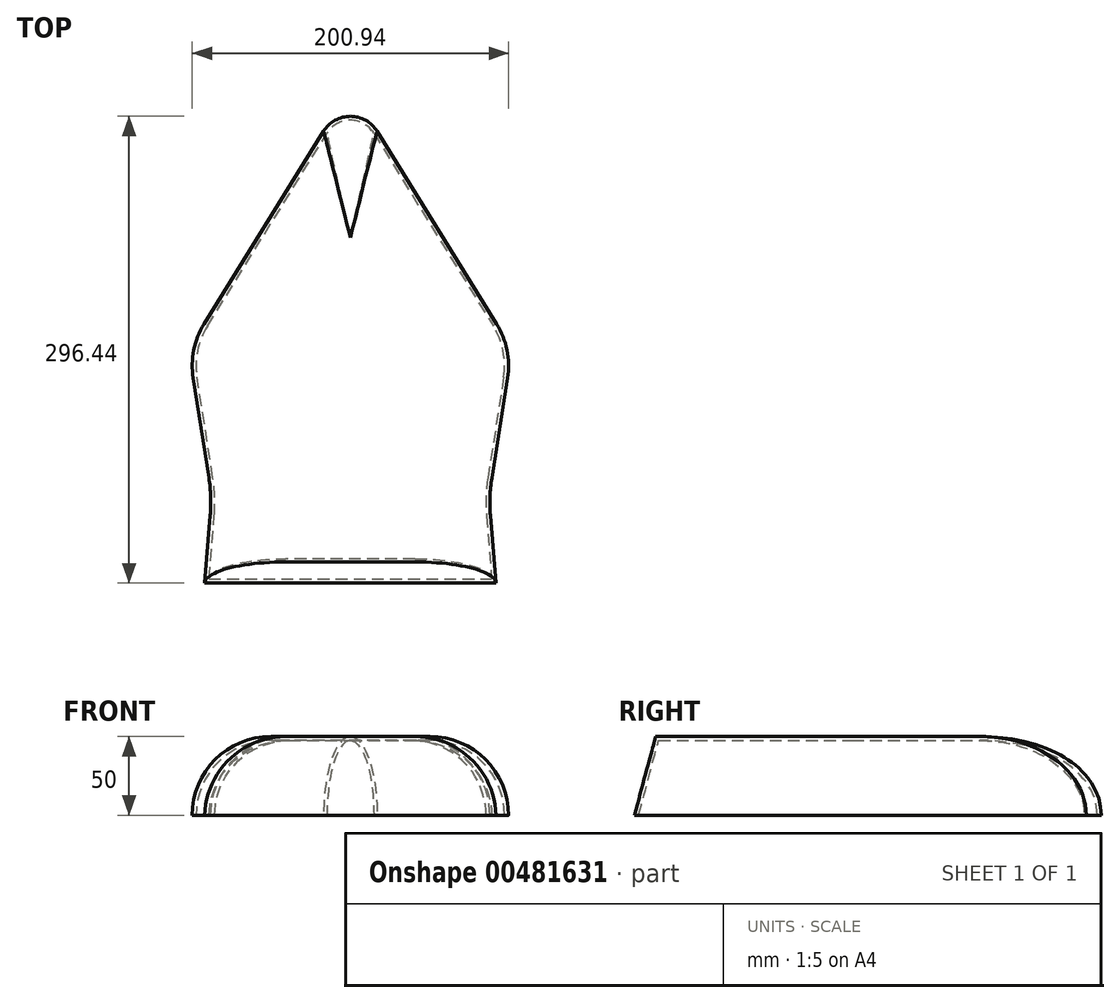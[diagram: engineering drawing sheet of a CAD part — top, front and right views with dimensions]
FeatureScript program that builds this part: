
annotation { "Feature Type Name" : "Feature", "Feature Type Description" : "" }
export const myFeature = defineFeature(function(context is Context, id is Id, definition is map)
    precondition{}
    {
        {
            var Q0;
            Q0=qCreatedBy(makeId("Top.planeOp"),FACE);
            var sketch = newSketch(context, id + "F0", { "sketchPlane" : qUnion([Q0])});
            skLineSegment(sketch, "E0", {"start": v(0, -100.69) * mm, "end": v(92.5, -100.69) * mm});
            skLineSegment(sketch, "E1", {"start": v(92.5, -100.69) * mm, "end": v(88.97, -57.8) * mm});
            skLineSegment(sketch, "E2", {"start": v(89.85, -34.06) * mm, "end": v(99.87, 29.64) * mm});
            skLineSegment(sketch, "E3", {"start": v(92.97, 63.75) * mm, "end": v(17, 186.29) * mm});
            skLineSegment(sketch, "E4.MirrorCS", {"start": v(-92.5, -100.69) * mm, "end": v(-88.97, -57.8) * mm});
            skLineSegment(sketch, "E5.MirrorCS", {"start": v(-89.85, -34.06) * mm, "end": v(-99.87, 29.64) * mm});
            skLineSegment(sketch, "E6.MirrorCS", {"start": v(0, -100.69) * mm, "end": v(-92.5, -100.69) * mm});
            skLineSegment(sketch, "E7.MirrorCS", {"start": v(-92.97, 63.75) * mm, "end": v(-17, 186.29) * mm});
            skPoint(sketch, "E8.visualSharp", {"position": v(0, 213.7) * mm});
            skArc(sketch, "E8.filletArc", {"start": v(17, 186.29) * mm, "mid": v(0, 195.75) * mm, "end": v(-17, 186.29) * mm});
            skPoint(sketch, "E9.visualSharp", {"position": v(-102.75, 47.97) * mm});
            skArc(sketch, "E9.filletArc", {"start": v(-92.97, 63.75) * mm, "mid": v(-99.48, 47.31) * mm, "end": v(-99.87, 29.64) * mm});
            skPoint(sketch, "E10.visualSharp", {"position": v(102.75, 47.97) * mm});
            skArc(sketch, "E10.filletArc", {"start": v(99.87, 29.64) * mm, "mid": v(99.48, 47.31) * mm, "end": v(92.97, 63.75) * mm});
            skPoint(sketch, "E11.visualSharp", {"position": v(-88, -45.87) * mm});
            skArc(sketch, "E11.filletArc", {"start": v(-88.97, -57.8) * mm, "mid": v(-88.7, -45.9) * mm, "end": v(-89.85, -34.06) * mm});
            skPoint(sketch, "E12.visualSharp", {"position": v(88, -45.87) * mm});
            skArc(sketch, "E12.filletArc", {"start": v(89.85, -34.06) * mm, "mid": v(88.7, -45.9) * mm, "end": v(88.97, -57.8) * mm});
            skSolve(sketch);
        }
        {
            var Q0;
            Q0=makeQuery(id+"F0.imprint","IMPRINT",FACE,{"disambiguationData":[TD([[makeQuery(id+"F0.imprint","IMPRINT",EDGE,{"derivedFrom":sQuery(id+"F0.wireOp",EDGE,"E0")}),1.0]])]});
            extrude(context, id + "F1", {"entities" : qUnion([Q0]), "depth" : 50 * mm});
        }
        {
            var Q0;
            Q0=makeQuery(id+"F1.opExtrude","CAP_EDGE",EDGE,{"disambiguationData":[OSD([sQuery(id+"F0.wireOp",EDGE,"E2")])],"isStart":false});
            var Q1;
            Q1=makeQuery(id+"F1.opExtrude","CAP_EDGE",EDGE,{"disambiguationData":[OSD([sQuery(id+"F0.wireOp",EDGE,"E12.filletArc")])],"isStart":false});
            var Q2;
            Q2=makeQuery(id+"F1.opExtrude","CAP_EDGE",EDGE,{"disambiguationData":[OSD([sQuery(id+"F0.wireOp",EDGE,"E1")])],"isStart":false});
            var Q3;
            Q3=makeQuery(id+"F1.opExtrude","CAP_EDGE",EDGE,{"disambiguationData":[OSD([sQuery(id+"F0.wireOp",EDGE,"E3")])],"isStart":false});
            var Q4;
            Q4=makeQuery(id+"F1.opExtrude","CAP_EDGE",EDGE,{"disambiguationData":[OSD([sQuery(id+"F0.wireOp",EDGE,"E10.filletArc")])],"isStart":false});
            var Q5;
            Q5=makeQuery(id+"F1.opExtrude","CAP_EDGE",EDGE,{"disambiguationData":[OSD([sQuery(id+"F0.wireOp",EDGE,"E8.filletArc")])],"isStart":false});
            var Q6;
            Q6=makeQuery(id+"F1.opExtrude","CAP_EDGE",EDGE,{"disambiguationData":[OSD([sQuery(id+"F0.wireOp",EDGE,"E7.MirrorCS")])],"isStart":false});
            var Q7;
            Q7=makeQuery(id+"F1.opExtrude","CAP_EDGE",EDGE,{"disambiguationData":[OSD([sQuery(id+"F0.wireOp",EDGE,"E9.filletArc")])],"isStart":false});
            var Q8;
            Q8=makeQuery(id+"F1.opExtrude","CAP_EDGE",EDGE,{"disambiguationData":[OSD([sQuery(id+"F0.wireOp",EDGE,"E5.MirrorCS")])],"isStart":false});
            var Q9;
            Q9=makeQuery(id+"F1.opExtrude","CAP_EDGE",EDGE,{"disambiguationData":[OSD([sQuery(id+"F0.wireOp",EDGE,"E11.filletArc")])],"isStart":false});
            var Q10;
            Q10=makeQuery(id+"F1.opExtrude","CAP_EDGE",EDGE,{"disambiguationData":[OSD([sQuery(id+"F0.wireOp",EDGE,"E4.MirrorCS")])],"isStart":false});
            fillet(context, id + "F2", {"entities" : qUnion([Q0, Q1, Q2, Q3, Q4, Q5, Q6, Q7, Q8, Q9, Q10]), "radius" : 50 * mm, "tangentPropagation" : true, "allowEdgeOverflow" : false});
        }
        {
            var Q0;
            Q0=makeQuery(id+"F1.opExtrude","CAP_EDGE",EDGE,{"disambiguationData":[OSD([sQuery(id+"F0.wireOp",EDGE,"E0"),sQuery(id+"F0.wireOp",EDGE,"E6.MirrorCS")])],"isStart":false});
            chamfer(context, id + "F3", {"entities" : qUnion([Q0]), "chamferType" : ChamferType.OFFSET_ANGLE, "width" : 50 * mm, "oppositeDirection" : false, "angle" : 15 * degree, "tangentPropagation" : true});
        }
        {
            var Q0;
            Q0=makeQuery(id+"F1.opExtrude","CAP_FACE",FACE,{"disambiguationData":[OSD([sQuery(id+"F0.wireOp",EDGE,"E0"),sQuery(id+"F0.wireOp",EDGE,"E1"),sQuery(id+"F0.wireOp",EDGE,"E2"),sQuery(id+"F0.wireOp",EDGE,"E3"),sQuery(id+"F0.wireOp",EDGE,"E4.MirrorCS"),sQuery(id+"F0.wireOp",EDGE,"E5.MirrorCS"),sQuery(id+"F0.wireOp",EDGE,"E6.MirrorCS"),sQuery(id+"F0.wireOp",EDGE,"E7.MirrorCS"),sQuery(id+"F0.wireOp",EDGE,"E8.filletArc"),sQuery(id+"F0.wireOp",EDGE,"E9.filletArc"),sQuery(id+"F0.wireOp",EDGE,"E10.filletArc"),sQuery(id+"F0.wireOp",EDGE,"E11.filletArc"),sQuery(id+"F0.wireOp",EDGE,"E12.filletArc")])],"isStart":true});
            shell(context, id + "F4", {"entities" : qUnion([Q0]), "thickness" : 2.5 * mm});
        }
    });
